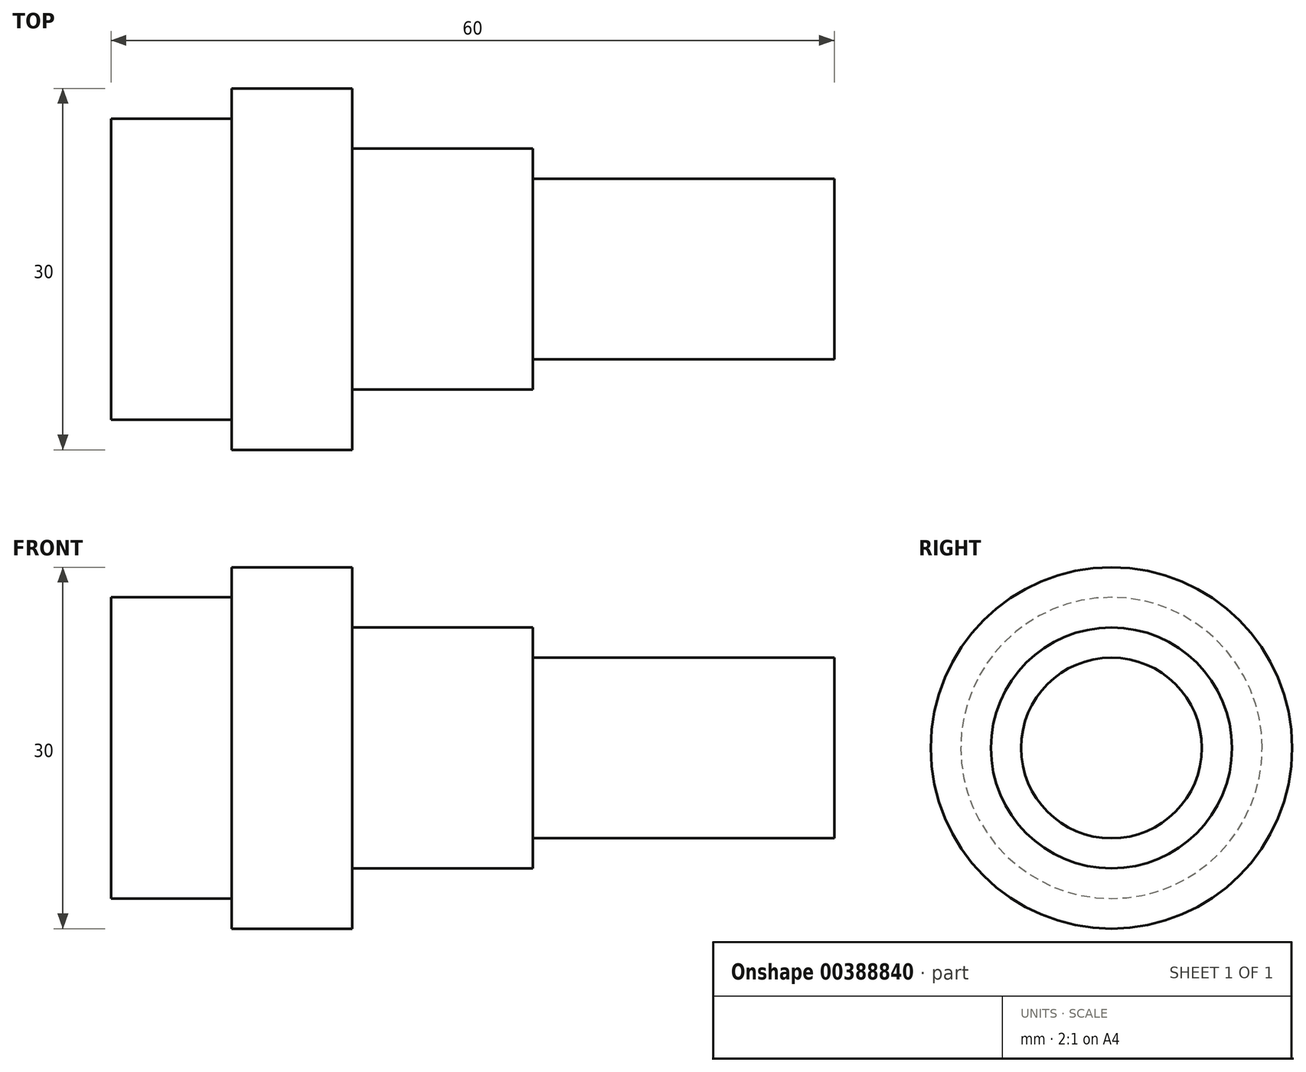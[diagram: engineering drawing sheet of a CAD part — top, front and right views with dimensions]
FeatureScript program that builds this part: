
annotation { "Feature Type Name" : "Feature", "Feature Type Description" : "" }
export const myFeature = defineFeature(function(context is Context, id is Id, definition is map)
    precondition{}
    {
        {
            var Q0;
            Q0=qCreatedBy(makeId("Front.planeOp"),FACE);
            var sketch = newSketch(context, id + "F0", { "sketchPlane" : qUnion([Q0])});
            skCircle(sketch, "E0", {"center": v(0, 0) * mm, "radius": 15 * mm});
            skSolve(sketch);
        }
        {
            var Q0;
            Q0 = qSketchRegion(id + "F0", true);
            extrude(context, id + "F1", {"entities" : qUnion([Q0]), "depth" : 10 * mm});
        }
        {
            var Q0;
            Q0=makeQuery(id+"F1.opExtrude","SWEPT_BODY",BODY,{"disambiguationData":[OSD([sQuery(id+"F0.wireOp",EDGE,"E0")])]});
            deleteBodies(context, id + "F2", {"entities" : qUnion([Q0])});
        }
        {
            var Q0;
            Q0=qCreatedBy(makeId("Right.planeOp"),FACE);
            var sketch = newSketch(context, id + "F3", { "sketchPlane" : qUnion([Q0])});
            skCircle(sketch, "E1", {"center": v(0, 0) * mm, "radius": 15 * mm});
            skSolve(sketch);
        }
        {
            var Q0;
            Q0=makeQuery(id+"F3.imprint","IMPRINT",FACE,{"disambiguationData":[TD([[makeQuery(id+"F3.imprint","IMPRINT",EDGE,{"derivedFrom":sQuery(id+"F3.wireOp",EDGE,"E1")}),1.0]])]});
            extrude(context, id + "F4", {"entities" : qUnion([Q0]), "depth" : 10 * mm});
        }
        {
            var Q0;
            Q0=makeQuery(id+"F4.opExtrude","CAP_FACE",FACE,{"disambiguationData":[OSD([sQuery(id+"F3.wireOp",EDGE,"E1")])],"isStart":false});
            var sketch = newSketch(context, id + "F5", { "sketchPlane" : qUnion([Q0])});
            skCircle(sketch, "E2", {"center": v(0, 0) * mm, "radius": 10 * mm});
            skSolve(sketch);
        }
        {
            var Q0;
            Q0=makeQuery(id+"F5.imprint","IMPRINT",FACE,{"disambiguationData":[TD([[makeQuery(id+"F5.imprint","IMPRINT",EDGE,{"derivedFrom":sQuery(id+"F5.wireOp",EDGE,"E2")}),1.0]])]});
            extrude(context, id + "F6", {"entities" : qUnion([Q0]), "operationType" : NewBodyOperationType.ADD, "depth" : 15 * mm});
        }
        {
            var Q0;
            Q0=makeQuery(id+"F6.opExtrude","CAP_FACE",FACE,{"disambiguationData":[OSD([sQuery(id+"F5.wireOp",EDGE,"E2")])],"isStart":false});
            var sketch = newSketch(context, id + "F7", { "sketchPlane" : qUnion([Q0])});
            skCircle(sketch, "E3", {"center": v(0, 0) * mm, "radius": 7.5 * mm});
            skSolve(sketch);
        }
        {
            var Q0;
            Q0=makeQuery(id+"F7.imprint","IMPRINT",FACE,{"disambiguationData":[TD([[makeQuery(id+"F7.imprint","IMPRINT",EDGE,{"derivedFrom":sQuery(id+"F7.wireOp",EDGE,"E3")}),1.0]])]});
            extrude(context, id + "F8", {"entities" : qUnion([Q0]), "operationType" : NewBodyOperationType.ADD, "depth" : 25 * mm});
        }
        {
            var Q0;
            Q0=makeQuery(id+"F4.opExtrude","CAP_FACE",FACE,{"disambiguationData":[OSD([sQuery(id+"F3.wireOp",EDGE,"E1")])],"isStart":true});
            var sketch = newSketch(context, id + "F9", { "sketchPlane" : qUnion([Q0])});
            skCircle(sketch, "E4", {"center": v(0, 0) * mm, "radius": 12.5 * mm});
            skSolve(sketch);
        }
        {
            var Q0;
            Q0 = qSketchRegion(id + "F9", true);
            extrude(context, id + "F10", {"entities" : qUnion([Q0]), "operationType" : NewBodyOperationType.ADD, "depth" : 10 * mm});
        }
    });
